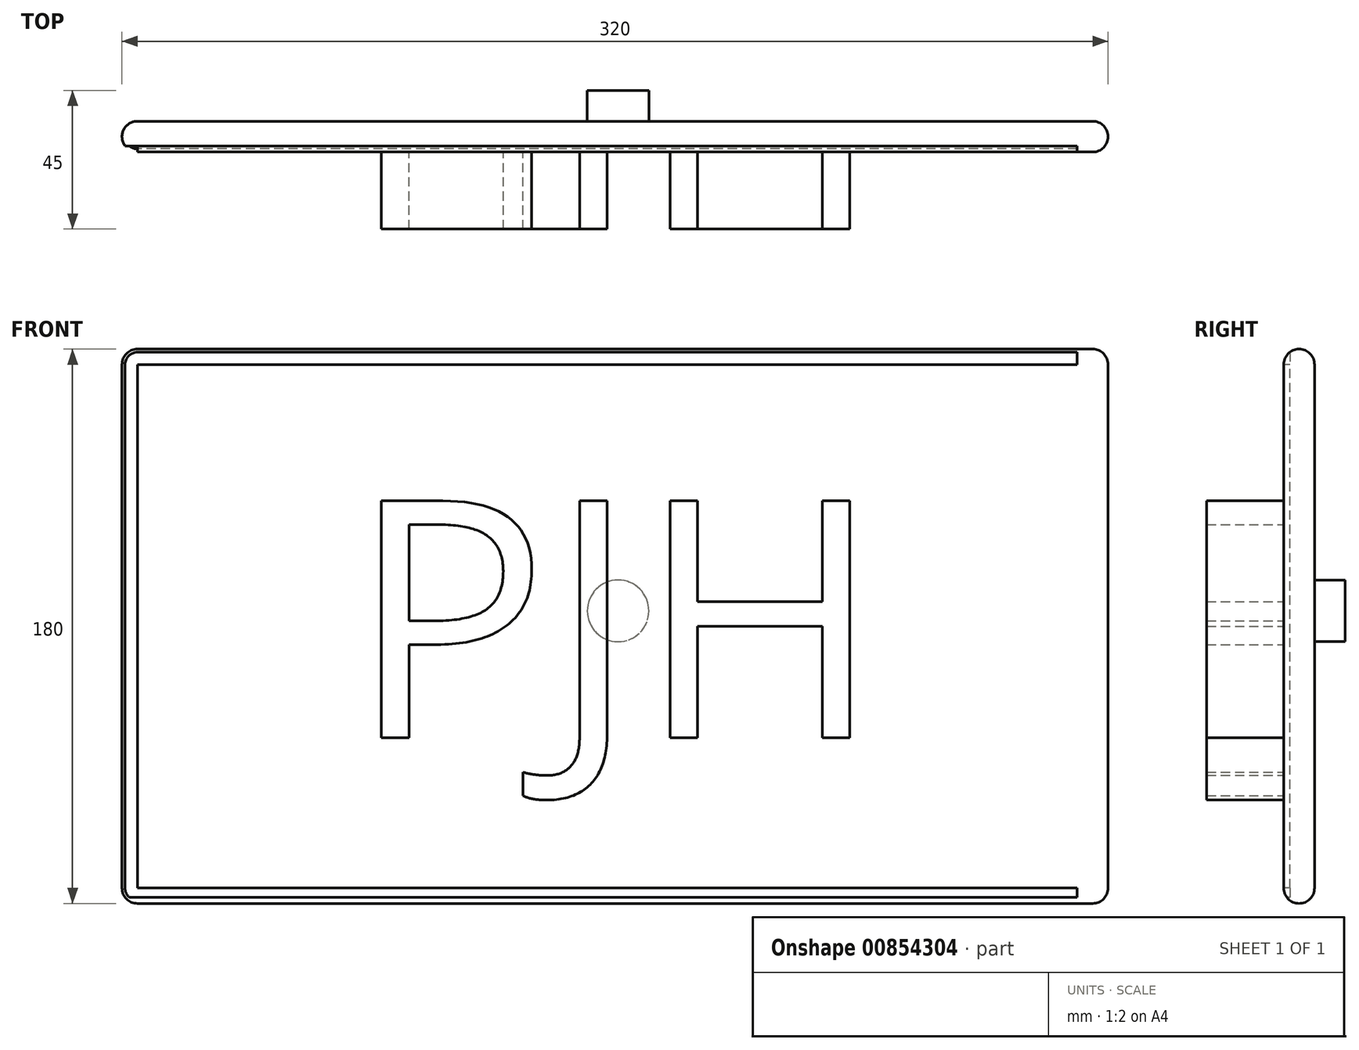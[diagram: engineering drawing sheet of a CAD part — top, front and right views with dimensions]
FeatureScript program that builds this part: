
annotation { "Feature Type Name" : "Feature", "Feature Type Description" : "" }
export const myFeature = defineFeature(function(context is Context, id is Id, definition is map)
    precondition{}
    {
        {
            var Q0;
            Q0=qCreatedBy(makeId("Front.planeOp"),FACE);
            var sketch = newSketch(context, id + "F0", { "sketchPlane" : qUnion([Q0])});
            skLineSegment(sketch, "E0.bottom", {"start": v(-3128.76, 152.95) * mm, "end": v(-2808.76, 152.95) * mm});
            skLineSegment(sketch, "E0.top", {"start": v(-3128.76, -27.05) * mm, "end": v(-2808.76, -27.05) * mm});
            skLineSegment(sketch, "E0.left", {"start": v(-3128.76, 152.95) * mm, "end": v(-3128.76, -27.05) * mm});
            skLineSegment(sketch, "E0.right", {"start": v(-2808.76, 152.95) * mm, "end": v(-2808.76, -27.05) * mm});
            skSolve(sketch);
        }
        {
            var Q0;
            Q0=makeQuery(id+"F0.imprint","IMPRINT",FACE,{"disambiguationData":[TD([[makeQuery(id+"F0.imprint","IMPRINT",EDGE,{"derivedFrom":sQuery(id+"F0.wireOp",EDGE,"E0.bottom")}),-1.0]])]});
            extrude(context, id + "F1", {"entities" : qUnion([Q0]), "depth" : 10 * mm, "offsetDistance" : 25 * mm});
        }
        {
            var Q0;
            Q0=makeQuery(id+"F1.opExtrude","SWEPT_EDGE",EDGE,{"disambiguationData":[OSD([sQuery(id+"F0.wireOp",EDGE,"E0.bottom"),sQuery(id+"F0.wireOp",EDGE,"E0.left")])]});
            var Q1;
            Q1=makeQuery(id+"F1.opExtrude","SWEPT_EDGE",EDGE,{"disambiguationData":[OSD([sQuery(id+"F0.wireOp",EDGE,"E0.top"),sQuery(id+"F0.wireOp",EDGE,"E0.left")])]});
            var Q2;
            Q2=makeQuery(id+"F1.opExtrude","SWEPT_EDGE",EDGE,{"disambiguationData":[OSD([sQuery(id+"F0.wireOp",EDGE,"E0.top"),sQuery(id+"F0.wireOp",EDGE,"E0.right")])]});
            var Q3;
            Q3=makeQuery(id+"F1.opExtrude","SWEPT_EDGE",EDGE,{"disambiguationData":[OSD([sQuery(id+"F0.wireOp",EDGE,"E0.bottom"),sQuery(id+"F0.wireOp",EDGE,"E0.right")])]});
            var Q4;
            Q4=makeQuery(id+"F1.opExtrude","CAP_EDGE",EDGE,{"disambiguationData":[OSD([sQuery(id+"F0.wireOp",EDGE,"E0.bottom")])],"isStart":false});
            var Q5;
            Q5=makeQuery(id+"F1.opExtrude","CAP_EDGE",EDGE,{"disambiguationData":[OSD([sQuery(id+"F0.wireOp",EDGE,"E0.bottom")])],"isStart":true});
            var Q6;
            Q6=makeQuery(id+"F1.opExtrude","CAP_EDGE",EDGE,{"disambiguationData":[OSD([sQuery(id+"F0.wireOp",EDGE,"E0.left")])],"isStart":true});
            var Q7;
            Q7=makeQuery(id+"F1.opExtrude","CAP_EDGE",EDGE,{"disambiguationData":[OSD([sQuery(id+"F0.wireOp",EDGE,"E0.left")])],"isStart":false});
            var Q8;
            Q8=makeQuery(id+"F1.opExtrude","CAP_EDGE",EDGE,{"disambiguationData":[OSD([sQuery(id+"F0.wireOp",EDGE,"E0.right")])],"isStart":false});
            var Q9;
            Q9=makeQuery(id+"F1.opExtrude","CAP_EDGE",EDGE,{"disambiguationData":[OSD([sQuery(id+"F0.wireOp",EDGE,"E0.right")])],"isStart":true});
            var Q10;
            Q10=makeQuery(id+"F1.opExtrude","CAP_EDGE",EDGE,{"disambiguationData":[OSD([sQuery(id+"F0.wireOp",EDGE,"E0.top")])],"isStart":false});
            var Q11;
            Q11=makeQuery(id+"F1.opExtrude","CAP_EDGE",EDGE,{"disambiguationData":[OSD([sQuery(id+"F0.wireOp",EDGE,"E0.top")])],"isStart":true});
            fillet(context, id + "F2", {"entities" : qUnion([Q0, Q1, Q2, Q3, Q4, Q5, Q6, Q7, Q8, Q9, Q10, Q11]), "radius" : 5 * mm, "tangentPropagation" : true, "allowEdgeOverflow" : false});
        }
        {
            var Q0;
            Q0=makeQuery(id+"F1.opExtrude","CAP_FACE",FACE,{"disambiguationData":[OSD([sQuery(id+"F0.wireOp",EDGE,"E0.bottom"),sQuery(id+"F0.wireOp",EDGE,"E0.top"),sQuery(id+"F0.wireOp",EDGE,"E0.left"),sQuery(id+"F0.wireOp",EDGE,"E0.right")])],"isStart":false});
            var sketch = newSketch(context, id + "F3", { "sketchPlane" : qUnion([Q0])});
            skLineSegment(sketch, "E1.bottom", {"start": v(-3136.76, 152.95) * mm, "end": v(-2818.76, 152.95) * mm});
            skLineSegment(sketch, "E1.top", {"start": v(-3136.76, -25.05) * mm, "end": v(-2818.76, -25.05) * mm});
            skLineSegment(sketch, "E1.left", {"start": v(-3136.76, 152.95) * mm, "end": v(-3136.76, -25.05) * mm});
            skLineSegment(sketch, "E1.right", {"start": v(-2818.76, 152.95) * mm, "end": v(-2818.76, -25.05) * mm});
            skSolve(sketch);
        }
        {
            var Q0;
            {var subQ0=sQuery(id+"F3.wireOp",EDGE,"E1.top");Q0=makeQuery(id+"F3.imprint","IMPRINT",FACE,{"disambiguationData":[TD([[makeQuery(id+"F3.imprint","IMPRINT",EDGE,{"derivedFrom":subQ0}),1.0]])]});}
            extrude(context, id + "F4", {"entities" : qUnion([Q0]), "operationType" : NewBodyOperationType.REMOVE, "oppositeDirection" : true, "depth" : 2 * mm, "offsetDistance" : 25 * mm});
        }
        {
            var Q0;
            Q0=makeQuery(id+"F1.opExtrude","CAP_FACE",FACE,{"disambiguationData":[OSD([sQuery(id+"F0.wireOp",EDGE,"E0.bottom"),sQuery(id+"F0.wireOp",EDGE,"E0.top"),sQuery(id+"F0.wireOp",EDGE,"E0.left"),sQuery(id+"F0.wireOp",EDGE,"E0.right")])],"isStart":true});
            var sketch = newSketch(context, id + "F5", { "sketchPlane" : qUnion([Q0])});
            skCircle(sketch, "E2", {"center": v(2967.76, 67.95) * mm, "radius": 10 * mm});
            skSolve(sketch);
        }
        {
            var Q0;
            Q0=makeQuery(id+"F5.imprint","IMPRINT",FACE,{"disambiguationData":[TD([[makeQuery(id+"F5.imprint","IMPRINT",EDGE,{"derivedFrom":sQuery(id+"F5.wireOp",EDGE,"E2")}),1.0]])]});
            extrude(context, id + "F6", {"entities" : qUnion([Q0]), "operationType" : NewBodyOperationType.ADD, "depth" : 10 * mm, "offsetDistance" : 25 * mm});
        }
        {
            var Q0;
            Q0=makeQuery(id+"F1.opExtrude","CAP_FACE",FACE,{"disambiguationData":[OSD([sQuery(id+"F0.wireOp",EDGE,"E0.bottom"),sQuery(id+"F0.wireOp",EDGE,"E0.top"),sQuery(id+"F0.wireOp",EDGE,"E0.left"),sQuery(id+"F0.wireOp",EDGE,"E0.right")])],"isStart":false});
            var sketch = newSketch(context, id + "F7", { "sketchPlane" : qUnion([Q0])});
            skText(sketch, "E3", { "text": "PJH", "fontName": "OpenSans-Regular.ttf"});
            const initialGuessF7  = {"E3": [-3.05513, 0.02677, 1, 0, 0.07757]};
            skSetInitialGuess(sketch, initialGuessF7);
            skSolve(sketch);
        }
        {
            var Q0;
            Q0=makeQuery(id+"F7.imprint","IMPRINT",FACE,{"disambiguationData":[TD([[makeQuery(id+"F7.imprint","IMPRINT",EDGE,{"derivedFrom":sQuery(id+"F7.wireOp",EDGE,"E3.sketch_text.stroke-15")}),-1.0]])]});
            var Q1;
            Q1=makeQuery(id+"F7.imprint","IMPRINT",FACE,{"disambiguationData":[TD([[makeQuery(id+"F7.imprint","IMPRINT",EDGE,{"derivedFrom":sQuery(id+"F7.wireOp",EDGE,"E3.sketch_text.stroke-25")}),-1.0]])]});
            var Q2;
            Q2=makeQuery(id+"F7.imprint","IMPRINT",FACE,{"disambiguationData":[TD([[makeQuery(id+"F7.imprint","IMPRINT",EDGE,{"derivedFrom":sQuery(id+"F7.wireOp",EDGE,"E3.sketch_text.stroke-0")}),-1.0]])]});
            extrude(context, id + "F8", {"entities" : qUnion([Q0, Q1, Q2]), "operationType" : NewBodyOperationType.ADD, "depth" : 25 * mm, "offsetDistance" : 25 * mm});
        }
    });
